# Revit family: 1. Doré_NormalP_EN
name_source: partatom
category: Modelos genéricos
revit_build: Autodesk Revit LT 2017 (Build: 20160225_1515(x64)
units: mm (PartAtom-declared; Revit-internal decimal feet)

## family parameters
Anfitrión = Muro
Compartido = No
Corte con vacíos al cargar = No
Cota de conector redondo = Diámetro de uso
Puede alojar armadura = No
Punto de cálculo de habitación = No
Siempre vertical = Sí
Tipo de pieza = Normal

## types (1)
- Stonepanel® Doré 20 cm - 60 cm
    Absorption = Low absorption
    Anchor system = Perforated steel banding:
- Stainless steel grade AISI 316 (1.4401) or AISI 304 (1.4301) with a minimum thickness of 0.7 mm and width of 12 mm to 15 mm, with holes 6±1 mm in diameter.
- Stainless steel grade AISI 304 (1.4301) with a minimum thickness of 0.8 mm and width of 10±1 mm, with holes 5±1 mm in diameter.
- The steel banding has five holes on each of the two wings, which are aligned in order to fix a screw through both holes into the wall.

Stainless steel screws and wall plugs:
The pull-out value of the fixings for securing Stonepanel Sky panels to the wall should be determined on site using the characteristic pull-out resistance divided by a minimum safety factor of 3.
Perforated steel banding:
- Stainless steel grade AISI 316 (1.4401) or AISI 304 (1.4301) with a minimum thickness of 0.7 mm and width of 12 mm to 15 mm, with holes 6±1 mm in diameter.
- Stainless steel grade AISI 304 (1.4301) with a minimum thickness of 0.8 mm and width of 10±1 mm, with holes 5±1 mm in diameter.
- The steel banding has five holes on each of the two wings, which are aligned in order to fix a screw through both holes into the wall.

Stainless steel screws and wall plugs:
The pull-out value of the fixings for securing Stonepanel Sky panels to the wall should be determined on site using the characteristic pull-out resistance divided by a minimum safety factor of 3.
    Apparent Density = 79,5 kg/m2
    Aspect = Contemporary
    Certifications = Avis Technique
    Cleaning = Generally the panels do not require maintenance and are self-cleaning but removal of some types of mark may require specialist treatment
For abnormal soiling, the surface may be cleaned using a hot water/household detergent mixture, applied
with a suitable cleaning pad or sponge.
    Construction details = Details of:
- Installation with a metal profile
- Installation of Stonepanel
- Installation on interior wall
- Installation of the safety element (perforated band, screws and wall plugs)
- Incoming corner
- Protruding corner
- Prefabricated protruding corner
- Protruding corner with sawn panels
- Protruding corner without Stonepanel continuity (lateral façade)
- Upper edges
- Avobe parapet
- Frame of vain
    Delivery form = Panels are packed in plastic in pairs.
    Descripción = Panel made of natural stones bonded to a cement base reinforced with glassfibre mesh
    Durability = The system has a design life in excess of 30 years.
    Fabricante = Cupastone
    Finish = Natural
    Fire resistance = A1 Non-combustible
    Form = “S”-shaped
    Format = 600 x 200
    Height = 200 mm  [stored 0.656168 ft]
    Height offset = 0 mm  [stored 0 ft]
    Imagen de tipo = <Ninguno>
    Large = 600 mm
    Material = Golden quartzite with brown and grey tones, that creates an elegant and bright look for modern and rustic projects.
    Modelo = Stonepanel® Doré
    Other relevant info = All panels installed above 2 m from the ground must be fixed with both mortar adhesive and mechanical fixings
    Oxidation = No oxidation
    Principal colour = Gold
    Resistance = High resistance
    Secondary colour = Grey
    Stonepanel advantages = More Efficient: Simple and quick installation: 10 times faster than traditional masonry (placing rate average 20m2/day). More profitable: virtually non-existent product waste. Natural Stone products are more durable than other cladding materials. Stonepanel™ installation requires no skilled labour or machinery.
Safer: The incorporated mechanical anchor of Stonepanel™, made of stainless steel, enables the installation of natural stone panel on surfaces higher than two meters. Strong and uniform cement base ensures adherence and allows piece cutting without risk of detachment.
High Quality: Manufacturing processes are continually monitored by the R&D Department of CUPAGROUP. A great selection of natural stone is done by the experts of CUPASTONE. Special pieces are available, such as corners (solid, straight end, double end or for windows), coverings and other complementary solutions.
More Aesthetic: ‘S’-shaped panels to avoid visible joints, in order to enhance the external look of any projet. A wide range of natural stone panels with different colours and finishes is available. Beauty and exclusiveness of the natural stone: each piece is unique.
    Tests performed by Avis Technique = Avis Technique
Mechanical strenth of the anchor
Resistance of the mechanical fixing
Testing of durability after water
Durability after freeze
Seismic test
Fire test
    URL = http://www.cupastone.com
    Uses Indicated = Decorative cladding system suitable for indoor and outdoor use on new or existing buildings when attached to solid walls of masonry or concrete.
    Weight = 8,75 kg
    Width = 50 mm  [stored 0.164042 ft]

note: [stored X ft] marks values corroborated as IEEE doubles in the binary element streams (Revit-internal decimal feet)
